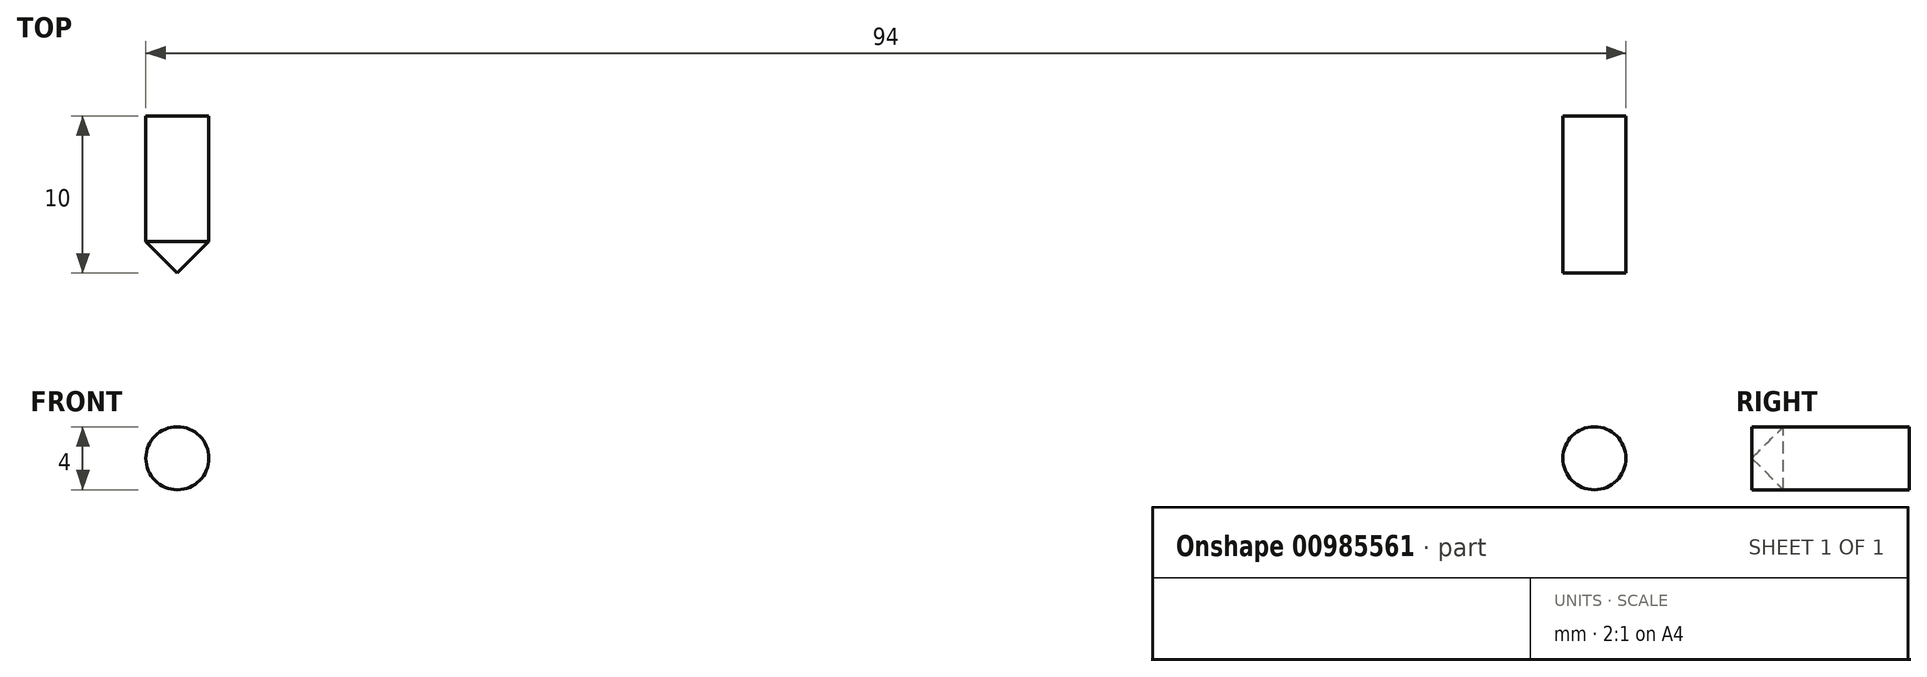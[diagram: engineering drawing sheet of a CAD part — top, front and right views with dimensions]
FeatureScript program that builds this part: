
annotation { "Feature Type Name" : "Feature", "Feature Type Description" : "" }
export const myFeature = defineFeature(function(context is Context, id is Id, definition is map)
    precondition{}
    {
        {
            var Q0;
            Q0=qCreatedBy(makeId("Front.planeOp"),FACE);
            var sketch = newSketch(context, id + "F0", { "sketchPlane" : qUnion([Q0])});
            skLineSegment(sketch, "E0.bottom", {"start": v(75, -25) * mm, "end": v(-75, -25) * mm});
            skLineSegment(sketch, "E0.top", {"start": v(75, 25) * mm, "end": v(-75, 25) * mm});
            skLineSegment(sketch, "E0.left", {"start": v(75, -25) * mm, "end": v(75, 25) * mm});
            skLineSegment(sketch, "E0.right", {"start": v(-75, -25) * mm, "end": v(-75, 25) * mm});
            skPoint(sketch, "E0.middle", {"position": v(0, 0) * mm});
            skSolve(sketch);
        }
        {
            var Q0;
            Q0 = qSketchRegion(id + "F0", true);
            extrude(context, id + "F1", {"entities" : qUnion([Q0]), "depth" : 10 * mm, "offsetDistance" : 25.4 * mm});
        }
        {
            var Q0;
            Q0=makeQuery(id+"F1.opExtrude","CAP_FACE",FACE,{"disambiguationData":[OSD([sQuery(id+"F0.wireOp",EDGE,"E0.bottom"),sQuery(id+"F0.wireOp",EDGE,"E0.top"),sQuery(id+"F0.wireOp",EDGE,"E0.left"),sQuery(id+"F0.wireOp",EDGE,"E0.right")])],"isStart":false});
            var sketch = newSketch(context, id + "F2", { "sketchPlane" : qUnion([Q0])});
            skLineSegment(sketch, "E1", {"start": v(-169.2, -5) * mm, "end": v(171.9, -5) * mm});
            skCircle(sketch, "E2", {"center": v(-60, -5) * mm, "radius": 2 * mm});
            skCircle(sketch, "E3", {"center": v(-30, -5) * mm, "radius": 2 * mm});
            skCircle(sketch, "E4", {"center": v(30, -5) * mm, "radius": 2 * mm});
            skCircle(sketch, "E5", {"center": v(60, -5) * mm, "radius": 2 * mm});
            skLineSegment(sketch, "E6", {"start": v(0, 48.32) * mm, "end": v(0, -50.1) * mm});
            skPoint(sketch, "E6.startSnap0", {"position": v(0, 25) * mm});
            skSolve(sketch);
        }
        {
            var Q0;
            {var subQ0=sQuery(id+"F2.wireOp",EDGE,"E3");var subQ1=sQuery(id+"F2.wireOp",EDGE,"E1");var subQ2=makeQuery(id+"F2.imprint","INTERSECT",VERTEX,{"disambiguationData":[OD(0.0)],"derivedFrom":[subQ1,subQ0]});Q0=makeQuery(id+"F2.imprint","IMPRINT",FACE,{"disambiguationData":[TD([[makeQuery(id+"F2.imprint","IMPRINT",EDGE,{"disambiguationData":[TD([[subQ2,-1.0]])],"derivedFrom":subQ1}),1.0]])]});}
            var Q1;
            {var subQ0=sQuery(id+"F2.wireOp",EDGE,"E3");var subQ1=sQuery(id+"F2.wireOp",EDGE,"E1");var subQ2=makeQuery(id+"F2.imprint","INTERSECT",VERTEX,{"disambiguationData":[OD(0.0)],"derivedFrom":[subQ1,subQ0]});Q1=makeQuery(id+"F2.imprint","IMPRINT",FACE,{"disambiguationData":[TD([[makeQuery(id+"F2.imprint","IMPRINT",EDGE,{"disambiguationData":[TD([[subQ2,-1.0]])],"derivedFrom":subQ1}),-1.0]])]});}
            var Q2;
            {var subQ0=sQuery(id+"F2.wireOp",EDGE,"E2");var subQ1=sQuery(id+"F2.wireOp",EDGE,"E1");var subQ2=makeQuery(id+"F2.imprint","INTERSECT",VERTEX,{"disambiguationData":[OD(0.0)],"derivedFrom":[subQ1,subQ0]});Q2=makeQuery(id+"F2.imprint","IMPRINT",FACE,{"disambiguationData":[TD([[makeQuery(id+"F2.imprint","IMPRINT",EDGE,{"disambiguationData":[TD([[subQ2,-1.0]])],"derivedFrom":subQ1}),1.0]])]});}
            var Q3;
            {var subQ0=sQuery(id+"F2.wireOp",EDGE,"E2");var subQ1=sQuery(id+"F2.wireOp",EDGE,"E1");var subQ2=makeQuery(id+"F2.imprint","INTERSECT",VERTEX,{"disambiguationData":[OD(0.0)],"derivedFrom":[subQ1,subQ0]});Q3=makeQuery(id+"F2.imprint","IMPRINT",FACE,{"disambiguationData":[TD([[makeQuery(id+"F2.imprint","IMPRINT",EDGE,{"disambiguationData":[TD([[subQ2,-1.0]])],"derivedFrom":subQ1}),-1.0]])]});}
            var Q4;
            {var subQ0=sQuery(id+"F2.wireOp",EDGE,"E4");var subQ1=sQuery(id+"F2.wireOp",EDGE,"E1");var subQ2=makeQuery(id+"F2.imprint","INTERSECT",VERTEX,{"disambiguationData":[OD(0.0)],"derivedFrom":[subQ1,subQ0]});Q4=makeQuery(id+"F2.imprint","IMPRINT",FACE,{"disambiguationData":[TD([[makeQuery(id+"F2.imprint","IMPRINT",EDGE,{"disambiguationData":[TD([[subQ2,-1.0]])],"derivedFrom":subQ1}),1.0]])]});}
            var Q5;
            {var subQ0=sQuery(id+"F2.wireOp",EDGE,"E4");var subQ1=sQuery(id+"F2.wireOp",EDGE,"E1");var subQ2=makeQuery(id+"F2.imprint","INTERSECT",VERTEX,{"disambiguationData":[OD(0.0)],"derivedFrom":[subQ1,subQ0]});Q5=makeQuery(id+"F2.imprint","IMPRINT",FACE,{"disambiguationData":[TD([[makeQuery(id+"F2.imprint","IMPRINT",EDGE,{"disambiguationData":[TD([[subQ2,-1.0]])],"derivedFrom":subQ1}),-1.0]])]});}
            var Q6;
            {var subQ0=sQuery(id+"F2.wireOp",EDGE,"E5");var subQ1=sQuery(id+"F2.wireOp",EDGE,"E1");var subQ2=makeQuery(id+"F2.imprint","INTERSECT",VERTEX,{"disambiguationData":[OD(0.0)],"derivedFrom":[subQ1,subQ0]});Q6=makeQuery(id+"F2.imprint","IMPRINT",FACE,{"disambiguationData":[TD([[makeQuery(id+"F2.imprint","IMPRINT",EDGE,{"disambiguationData":[TD([[subQ2,-1.0]])],"derivedFrom":subQ1}),1.0]])]});}
            var Q7;
            {var subQ0=sQuery(id+"F2.wireOp",EDGE,"E5");var subQ1=sQuery(id+"F2.wireOp",EDGE,"E1");var subQ2=makeQuery(id+"F2.imprint","INTERSECT",VERTEX,{"disambiguationData":[OD(0.0)],"derivedFrom":[subQ1,subQ0]});Q7=makeQuery(id+"F2.imprint","IMPRINT",FACE,{"disambiguationData":[TD([[makeQuery(id+"F2.imprint","IMPRINT",EDGE,{"disambiguationData":[TD([[subQ2,-1.0]])],"derivedFrom":subQ1}),-1.0]])]});}
            extrude(context, id + "F3", {"entities" : qUnion([Q0, Q1, Q2, Q3, Q4, Q5, Q6, Q7]), "operationType" : NewBodyOperationType.REMOVE, "endBound" : BoundingType.THROUGH_ALL, "oppositeDirection" : true, "depth" : 25.4 * mm, "offsetDistance" : 25.4 * mm});
        }
        {
            var Q0;
            Q0=makeQuery(id+"F3.boolean.opBoolean","COPY",EDGE,{"derivedFrom":makeQuery(id+"F3.opExtrude","CAP_EDGE",EDGE,{"disambiguationData":[OSD([sQuery(id+"F2.wireOp",EDGE,"E2")])],"isStart":true})});
            var Q1;
            Q1=makeQuery(id+"F3.boolean.opBoolean","COPY",EDGE,{"derivedFrom":makeQuery(id+"F3.opExtrude","CAP_EDGE",EDGE,{"disambiguationData":[OSD([sQuery(id+"F2.wireOp",EDGE,"E3")])],"isStart":true})});
            var Q2;
            Q2=makeQuery(id+"F3.boolean.opBoolean","COPY",EDGE,{"derivedFrom":makeQuery(id+"F3.opExtrude","CAP_EDGE",EDGE,{"disambiguationData":[OSD([sQuery(id+"F2.wireOp",EDGE,"E4")])],"isStart":true})});
            var Q3;
            Q3=makeQuery(id+"F3.boolean.opBoolean","COPY",EDGE,{"derivedFrom":makeQuery(id+"F3.opExtrude","CAP_EDGE",EDGE,{"disambiguationData":[OSD([sQuery(id+"F2.wireOp",EDGE,"E5")])],"isStart":true})});
            chamfer(context, id + "F4", {"entities" : qUnion([Q0, Q1, Q2, Q3]), "width" : 2 * mm, "tangentPropagation" : true});
        }
    });
